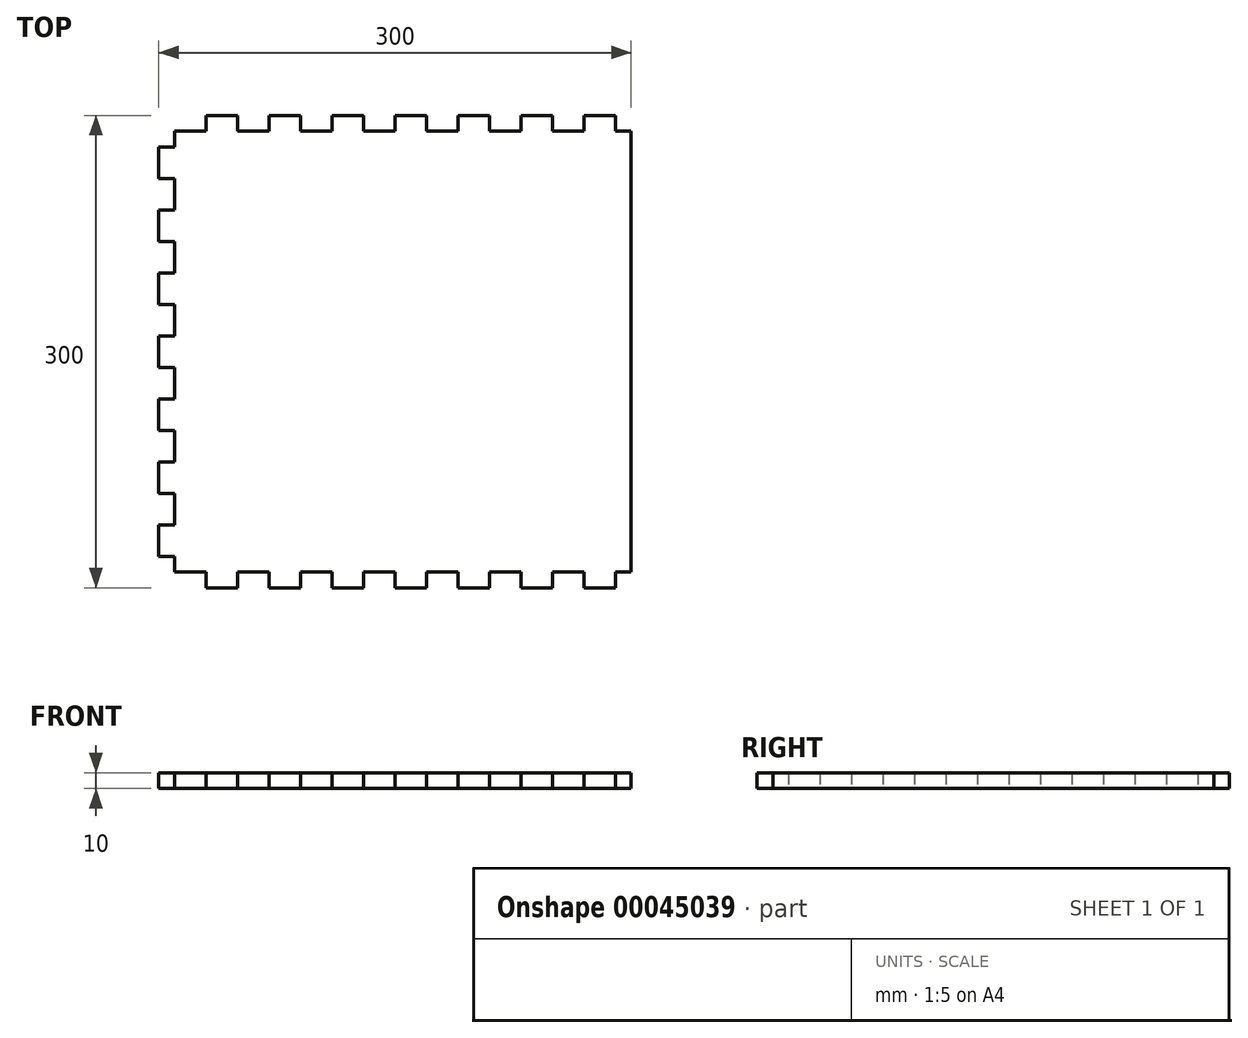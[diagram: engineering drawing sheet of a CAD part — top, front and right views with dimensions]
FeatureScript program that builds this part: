
annotation { "Feature Type Name" : "Feature", "Feature Type Description" : "" }
export const myFeature = defineFeature(function(context is Context, id is Id, definition is map)
    precondition{}
    {
        {
            var Q0;
            Q0=qCreatedBy(makeId("Top.planeOp"),FACE);
            var sketch = newSketch(context, id + "F0", { "sketchPlane" : qUnion([Q0])});
            skLineSegment(sketch, "E0.bottom", {"start": v(0, 0) * mm, "end": v(300, 0) * mm});
            skLineSegment(sketch, "E0.top", {"start": v(0, 300) * mm, "end": v(300, 300) * mm});
            skLineSegment(sketch, "E0.left", {"start": v(0, 0) * mm, "end": v(0, 300) * mm});
            skLineSegment(sketch, "E0.right", {"start": v(300, 0) * mm, "end": v(300, 300) * mm});
            skSolve(sketch);
        }
        {
            var Q0;
            Q0=qSketchRegion(id+"F0",true);
            extrude(context, id + "F1", {"entities" : qUnion([Q0]), "depth" : 10 * mm});
        }
        {
            var Q0;
            Q0=makeQuery(id+"F0.imprint","IMPRINT",FACE,{"disambiguationData":[TD([[makeQuery(id+"F0.imprint","IMPRINT",EDGE,{"derivedFrom":sQuery(id+"F0.wireOp",EDGE,"E0.bottom")}),1.0]])]});
            var sketch = newSketch(context, id + "F2", { "sketchPlane" : qUnion([Q0])});
            skLineSegment(sketch, "E1.bottom", {"start": v(290, 290) * mm, "end": v(300, 290) * mm});
            skLineSegment(sketch, "E1.top", {"start": v(290, 300) * mm, "end": v(300, 300) * mm});
            skLineSegment(sketch, "E1.left", {"start": v(290, 290) * mm, "end": v(290, 300) * mm});
            skLineSegment(sketch, "E1.right", {"start": v(300, 290) * mm, "end": v(300, 300) * mm});
            skLineSegment(sketch, "E2.bottom", {"start": v(269.92, 290) * mm, "end": v(250, 290) * mm});
            skLineSegment(sketch, "E2.top", {"start": v(269.92, 300) * mm, "end": v(250, 300) * mm});
            skLineSegment(sketch, "E2.left", {"start": v(269.92, 290) * mm, "end": v(269.92, 300) * mm});
            skLineSegment(sketch, "E2.right", {"start": v(250, 290) * mm, "end": v(250, 300) * mm});
            skLineSegment(sketch, "E3.1.0.0", {"start": v(229.92, 290) * mm, "end": v(210, 290) * mm});
            skLineSegment(sketch, "E3.1.0.1", {"start": v(210, 290) * mm, "end": v(210, 300) * mm});
            skLineSegment(sketch, "E3.1.0.2", {"start": v(229.92, 290) * mm, "end": v(229.92, 300) * mm});
            skLineSegment(sketch, "E3.1.0.3", {"start": v(229.92, 300) * mm, "end": v(210, 300) * mm});
            skLineSegment(sketch, "E3.2.0.0", {"start": v(189.92, 290) * mm, "end": v(170, 290) * mm});
            skLineSegment(sketch, "E3.2.0.1", {"start": v(170, 290) * mm, "end": v(170, 300) * mm});
            skLineSegment(sketch, "E3.2.0.2", {"start": v(189.92, 290) * mm, "end": v(189.92, 300) * mm});
            skLineSegment(sketch, "E3.2.0.3", {"start": v(189.92, 300) * mm, "end": v(170, 300) * mm});
            skLineSegment(sketch, "E3.3.0.0", {"start": v(149.92, 290) * mm, "end": v(130, 290) * mm});
            skLineSegment(sketch, "E3.3.0.1", {"start": v(130, 290) * mm, "end": v(130, 300) * mm});
            skLineSegment(sketch, "E3.3.0.2", {"start": v(149.92, 290) * mm, "end": v(149.92, 300) * mm});
            skLineSegment(sketch, "E3.3.0.3", {"start": v(149.92, 300) * mm, "end": v(130, 300) * mm});
            skLineSegment(sketch, "E3.4.0.0", {"start": v(109.92, 290) * mm, "end": v(90, 290) * mm});
            skLineSegment(sketch, "E3.4.0.1", {"start": v(90, 290) * mm, "end": v(90, 300) * mm});
            skLineSegment(sketch, "E3.4.0.2", {"start": v(109.92, 290) * mm, "end": v(109.92, 300) * mm});
            skLineSegment(sketch, "E3.4.0.3", {"start": v(109.92, 300) * mm, "end": v(90, 300) * mm});
            skLineSegment(sketch, "E3.5.0.0", {"start": v(69.92, 290) * mm, "end": v(50, 290) * mm});
            skLineSegment(sketch, "E3.5.0.1", {"start": v(50, 290) * mm, "end": v(50, 300) * mm});
            skLineSegment(sketch, "E3.5.0.2", {"start": v(69.92, 290) * mm, "end": v(69.92, 300) * mm});
            skLineSegment(sketch, "E3.5.0.3", {"start": v(69.92, 300) * mm, "end": v(50, 300) * mm});
            skLineSegment(sketch, "E3.direction1", {"start": v(250, 290) * mm, "end": v(210, 290) * mm, "construction": true});
            skLineSegment(sketch, "E4.bottom", {"start": v(29.92, 300) * mm, "end": v(-24.56, 300) * mm});
            skLineSegment(sketch, "E4.top", {"start": v(29.92, 290) * mm, "end": v(-24.56, 290) * mm});
            skLineSegment(sketch, "E4.left", {"start": v(29.92, 300) * mm, "end": v(29.92, 290) * mm});
            skLineSegment(sketch, "E4.right", {"start": v(-24.56, 300) * mm, "end": v(-24.56, 290) * mm});
            skLineSegment(sketch, "E5.bottom", {"start": v(300, 10) * mm, "end": v(290, 10) * mm});
            skLineSegment(sketch, "E5.top", {"start": v(300, 0) * mm, "end": v(290, 0) * mm});
            skLineSegment(sketch, "E5.left", {"start": v(300, 10) * mm, "end": v(300, 0) * mm});
            skLineSegment(sketch, "E5.right", {"start": v(290, 10) * mm, "end": v(290, 0) * mm});
            skLineSegment(sketch, "E6.bottom", {"start": v(269.93, 0) * mm, "end": v(250, 0) * mm});
            skLineSegment(sketch, "E6.top", {"start": v(269.93, 10) * mm, "end": v(250, 10) * mm});
            skLineSegment(sketch, "E6.left", {"start": v(269.93, 0) * mm, "end": v(269.93, 10) * mm});
            skLineSegment(sketch, "E6.right", {"start": v(250, 0) * mm, "end": v(250, 10) * mm});
            skLineSegment(sketch, "E7.1.0.0", {"start": v(229.93, 0) * mm, "end": v(210, 0) * mm});
            skLineSegment(sketch, "E7.1.0.1", {"start": v(229.93, 10) * mm, "end": v(210, 10) * mm});
            skLineSegment(sketch, "E7.1.0.2", {"start": v(229.93, 0) * mm, "end": v(229.93, 10) * mm});
            skLineSegment(sketch, "E7.1.0.3", {"start": v(210, 0) * mm, "end": v(210, 10) * mm});
            skLineSegment(sketch, "E7.2.0.0", {"start": v(189.93, 0) * mm, "end": v(170, 0) * mm});
            skLineSegment(sketch, "E7.2.0.1", {"start": v(189.93, 10) * mm, "end": v(170, 10) * mm});
            skLineSegment(sketch, "E7.2.0.2", {"start": v(189.93, 0) * mm, "end": v(189.93, 10) * mm});
            skLineSegment(sketch, "E7.2.0.3", {"start": v(170, 0) * mm, "end": v(170, 10) * mm});
            skLineSegment(sketch, "E7.3.0.0", {"start": v(149.93, 0) * mm, "end": v(130, 0) * mm});
            skLineSegment(sketch, "E7.3.0.1", {"start": v(149.93, 10) * mm, "end": v(130, 10) * mm});
            skLineSegment(sketch, "E7.3.0.2", {"start": v(149.93, 0) * mm, "end": v(149.93, 10) * mm});
            skLineSegment(sketch, "E7.3.0.3", {"start": v(130, 0) * mm, "end": v(130, 10) * mm});
            skLineSegment(sketch, "E7.4.0.0", {"start": v(109.92, 0) * mm, "end": v(90, 0) * mm});
            skLineSegment(sketch, "E7.4.0.1", {"start": v(109.92, 10) * mm, "end": v(90, 10) * mm});
            skLineSegment(sketch, "E7.4.0.2", {"start": v(109.92, 0) * mm, "end": v(109.92, 10) * mm});
            skLineSegment(sketch, "E7.4.0.3", {"start": v(90, 0) * mm, "end": v(90, 10) * mm});
            skLineSegment(sketch, "E7.5.0.0", {"start": v(69.92, 0) * mm, "end": v(50, 0) * mm});
            skLineSegment(sketch, "E7.5.0.1", {"start": v(69.92, 10) * mm, "end": v(50, 10) * mm});
            skLineSegment(sketch, "E7.5.0.2", {"start": v(69.92, 0) * mm, "end": v(69.92, 10) * mm});
            skLineSegment(sketch, "E7.5.0.3", {"start": v(50, 0) * mm, "end": v(50, 10) * mm});
            skLineSegment(sketch, "E7.6.0.0", {"start": v(29.92, 0) * mm, "end": v(10, 0) * mm});
            skLineSegment(sketch, "E7.6.0.1", {"start": v(29.92, 10) * mm, "end": v(10, 10) * mm});
            skLineSegment(sketch, "E7.6.0.2", {"start": v(29.92, 0) * mm, "end": v(29.92, 10) * mm});
            skLineSegment(sketch, "E7.6.0.3", {"start": v(10, 0) * mm, "end": v(10, 10) * mm});
            skLineSegment(sketch, "E7.direction1", {"start": v(250, 0) * mm, "end": v(210, 0) * mm, "construction": true});
            skLineSegment(sketch, "E8.bottom", {"start": v(0, 0) * mm, "end": v(10, 0) * mm});
            skLineSegment(sketch, "E8.top", {"start": v(0, 19.93) * mm, "end": v(10, 19.93) * mm});
            skLineSegment(sketch, "E8.left", {"start": v(0, 0) * mm, "end": v(0, 19.93) * mm});
            skLineSegment(sketch, "E8.right", {"start": v(10, 0) * mm, "end": v(10, 19.93) * mm});
            skLineSegment(sketch, "E9.0.1.0", {"start": v(0, 40) * mm, "end": v(0, 59.93) * mm});
            skLineSegment(sketch, "E9.0.1.1", {"start": v(0, 40) * mm, "end": v(10, 40) * mm});
            skLineSegment(sketch, "E9.0.1.2", {"start": v(0, 59.93) * mm, "end": v(10, 59.93) * mm});
            skLineSegment(sketch, "E9.0.1.3", {"start": v(10, 40) * mm, "end": v(10, 59.93) * mm});
            skLineSegment(sketch, "E9.0.2.0", {"start": v(0, 80) * mm, "end": v(0, 99.93) * mm});
            skLineSegment(sketch, "E9.0.2.1", {"start": v(0, 80) * mm, "end": v(10, 80) * mm});
            skLineSegment(sketch, "E9.0.2.2", {"start": v(0, 99.93) * mm, "end": v(10, 99.93) * mm});
            skLineSegment(sketch, "E9.0.2.3", {"start": v(10, 80) * mm, "end": v(10, 99.93) * mm});
            skLineSegment(sketch, "E9.0.3.0", {"start": v(0, 120) * mm, "end": v(0, 139.92) * mm});
            skLineSegment(sketch, "E9.0.3.1", {"start": v(0, 120) * mm, "end": v(10, 120) * mm});
            skLineSegment(sketch, "E9.0.3.2", {"start": v(0, 139.92) * mm, "end": v(10, 139.92) * mm});
            skLineSegment(sketch, "E9.0.3.3", {"start": v(10, 120) * mm, "end": v(10, 139.92) * mm});
            skLineSegment(sketch, "E9.0.4.0", {"start": v(0, 160) * mm, "end": v(0, 179.93) * mm});
            skLineSegment(sketch, "E9.0.4.1", {"start": v(0, 160) * mm, "end": v(10, 160) * mm});
            skLineSegment(sketch, "E9.0.4.2", {"start": v(0, 179.93) * mm, "end": v(10, 179.93) * mm});
            skLineSegment(sketch, "E9.0.4.3", {"start": v(10, 160) * mm, "end": v(10, 179.93) * mm});
            skLineSegment(sketch, "E9.0.5.0", {"start": v(0, 200) * mm, "end": v(0, 219.93) * mm});
            skLineSegment(sketch, "E9.0.5.1", {"start": v(0, 200) * mm, "end": v(10, 200) * mm});
            skLineSegment(sketch, "E9.0.5.2", {"start": v(0, 219.93) * mm, "end": v(10, 219.93) * mm});
            skLineSegment(sketch, "E9.0.5.3", {"start": v(10, 200) * mm, "end": v(10, 219.93) * mm});
            skLineSegment(sketch, "E9.0.6.0", {"start": v(0, 240) * mm, "end": v(0, 259.93) * mm});
            skLineSegment(sketch, "E9.0.6.1", {"start": v(0, 240) * mm, "end": v(10, 240) * mm});
            skLineSegment(sketch, "E9.0.6.2", {"start": v(0, 259.93) * mm, "end": v(10, 259.93) * mm});
            skLineSegment(sketch, "E9.0.6.3", {"start": v(10, 240) * mm, "end": v(10, 259.93) * mm});
            skLineSegment(sketch, "E9.0.7.0", {"start": v(0, 280) * mm, "end": v(0, 299.93) * mm});
            skLineSegment(sketch, "E9.0.7.1", {"start": v(0, 280) * mm, "end": v(10, 280) * mm});
            skLineSegment(sketch, "E9.0.7.2", {"start": v(0, 299.93) * mm, "end": v(10, 299.93) * mm});
            skLineSegment(sketch, "E9.0.7.3", {"start": v(10, 280) * mm, "end": v(10, 299.93) * mm});
            skLineSegment(sketch, "E9.direction1", {"start": v(0, 0) * mm, "end": v(25, 0) * mm, "construction": true});
            skLineSegment(sketch, "E9.direction2", {"start": v(0, 0) * mm, "end": v(0, 40) * mm, "construction": true});
            skSolve(sketch);
        }
        {
            var Q0;
            Q0=qSketchRegion(id+"F2",true);
            var Q1;
            Q1=qConstructionFilter(qBodyType(qCreatedBy(id+"F2",EDGE),BodyType.WIRE),ConstructionObject.NO);
            extrude(context, id + "F3", {"entities" : qUnion([Q0]), "operationType" : NewBodyOperationType.REMOVE, "surfaceEntities" : qUnion([Q1]), "endBound" : BoundingType.THROUGH_ALL, "depth" : 25 * mm});
        }
    });
